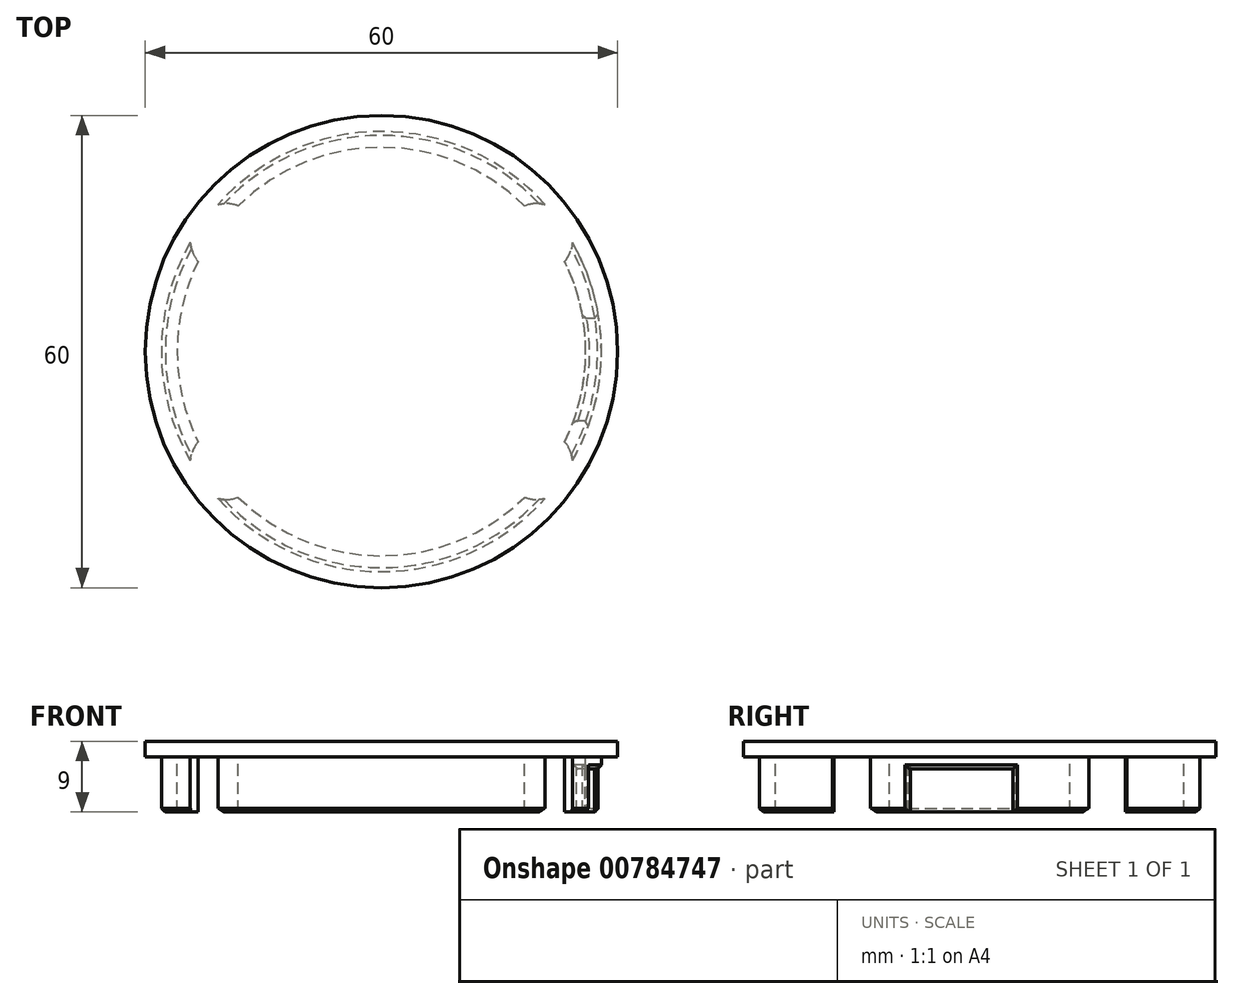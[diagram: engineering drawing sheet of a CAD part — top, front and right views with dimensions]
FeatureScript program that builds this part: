
annotation { "Feature Type Name" : "Feature", "Feature Type Description" : "" }
export const myFeature = defineFeature(function(context is Context, id is Id, definition is map)
    precondition{}
    {
        {
            var Q0;
            Q0=qCreatedBy(makeId("Top.planeOp"),FACE);
            var sketch = newSketch(context, id + "F0", { "sketchPlane" : qUnion([Q0])});
            skLineSegment(sketch, "E0.bottom", {"start": v(-22.5, 17.5) * mm, "end": v(22.5, 17.5) * mm, "construction": true});
            skLineSegment(sketch, "E0.top", {"start": v(-22.5, -17.5) * mm, "end": v(22.5, -17.5) * mm, "construction": true});
            skLineSegment(sketch, "E0.left", {"start": v(-22.5, 17.5) * mm, "end": v(-22.5, -17.5) * mm, "construction": true});
            skLineSegment(sketch, "E0.right", {"start": v(22.5, 17.5) * mm, "end": v(22.5, -17.5) * mm, "construction": true});
            skCircle(sketch, "E1", {"center": v(0, 0) * mm, "radius": 30 * mm});
            skLineSegment(sketch, "E2.bottom", {"start": v(-19.8, -14.3) * mm, "end": v(19.8, -14.3) * mm, "construction": true});
            skLineSegment(sketch, "E2.top", {"start": v(-19.8, 14.3) * mm, "end": v(19.8, 14.3) * mm, "construction": true});
            skLineSegment(sketch, "E2.left", {"start": v(-19.8, -14.3) * mm, "end": v(-19.8, 14.3) * mm, "construction": true});
            skLineSegment(sketch, "E2.right", {"start": v(19.8, -14.3) * mm, "end": v(19.8, 14.3) * mm, "construction": true});
            skSolve(sketch);
        }
        {
            var Q0;
            Q0 = qSketchRegion(id + "F0", true);
            extrude(context, id + "F1", {"entities" : qUnion([Q0]), "depth" : 2 * mm, "offsetDistance" : 25 * mm});
        }
        {
            var Q0;
            Q0=makeQuery(id+"F1.opExtrude","CAP_FACE",FACE,{"disambiguationData":[OSD([sQuery(id+"F0.wireOp",EDGE,"E1")])],"isStart":true});
            var sketch = newSketch(context, id + "F2", { "sketchPlane" : qUnion([Q0])});
            skCircle(sketch, "E3", {"center": v(0, 0) * mm, "radius": 27.95 * mm});
            skSolve(sketch);
        }
        {
            var Q0;
            Q0 = qSketchRegion(id + "F2", true);
            extrude(context, id + "F3", {"entities" : qUnion([Q0]), "operationType" : NewBodyOperationType.ADD, "depth" : 7 * mm, "offsetDistance" : 25 * mm});
        }
        {
            var Q0;
            Q0=makeQuery(id+"F3.opExtrude","CAP_FACE",FACE,{"disambiguationData":[OSD([sQuery(id+"F2.wireOp",EDGE,"E3")])],"isStart":false});
            shell(context, id + "F4", {"entities" : qUnion([Q0]), "thickness" : 2 * mm});
        }
        {
            var Q0;
            Q0=qCreatedBy(makeId("Right.planeOp"),FACE);
            var sketch = newSketch(context, id + "F5", { "sketchPlane" : qUnion([Q0])});
            skLineSegment(sketch, "E4.bottom", {"start": v(4.2, -11.5) * mm, "end": v(-8.8, -11.5) * mm});
            skLineSegment(sketch, "E4.top", {"start": v(4.2, -1.5) * mm, "end": v(-8.8, -1.5) * mm});
            skLineSegment(sketch, "E4.left", {"start": v(4.2, -11.5) * mm, "end": v(4.2, -1.5) * mm});
            skLineSegment(sketch, "E4.right", {"start": v(-8.8, -11.5) * mm, "end": v(-8.8, -1.5) * mm});
            skSolve(sketch);
        }
        {
            var Q0;
            Q0 = qSketchRegion(id + "F5", true);
            extrude(context, id + "F6", {"entities" : qUnion([Q0]), "operationType" : NewBodyOperationType.REMOVE, "depth" : 30 * mm, "offsetDistance" : 25 * mm});
        }
        {
            var Q0;
            Q0=makeQuery(id+"F6.boolean.opBoolean","INTERSECT",EDGE,{"derivedFrom":[makeQuery(id+"F3.opExtrude","SWEPT_FACE",FACE,{"disambiguationData":[OSD([sQuery(id+"F2.wireOp",EDGE,"E3")])]}),makeQuery(id+"F6.opExtrude","SWEPT_FACE",FACE,{"disambiguationData":[OSD([sQuery(id+"F5.wireOp",EDGE,"E4.top")])]})]});
            var Q1;
            Q1=makeQuery(id+"F6.boolean.opBoolean","INTERSECT",EDGE,{"derivedFrom":[makeQuery(id+"F3.opExtrude","SWEPT_FACE",FACE,{"disambiguationData":[OSD([sQuery(id+"F2.wireOp",EDGE,"E3")])]}),makeQuery(id+"F6.opExtrude","SWEPT_FACE",FACE,{"disambiguationData":[OSD([sQuery(id+"F5.wireOp",EDGE,"E4.right")])]})]});
            var Q2;
            Q2=makeQuery(id+"F6.boolean.opBoolean","INTERSECT",EDGE,{"derivedFrom":[makeQuery(id+"F4.opShell","OFFSET_FACE",FACE,{"disambiguationData":[OSD([sQuery(id+"F2.wireOp",EDGE,"E3")])]}),makeQuery(id+"F6.opExtrude","SWEPT_FACE",FACE,{"disambiguationData":[OSD([sQuery(id+"F5.wireOp",EDGE,"E4.top")])]})]});
            var Q3;
            Q3=makeQuery(id+"F6.boolean.opBoolean","INTERSECT",EDGE,{"derivedFrom":[makeQuery(id+"F4.opShell","OFFSET_FACE",FACE,{"disambiguationData":[OSD([sQuery(id+"F2.wireOp",EDGE,"E3")])]}),makeQuery(id+"F6.opExtrude","SWEPT_FACE",FACE,{"disambiguationData":[OSD([sQuery(id+"F5.wireOp",EDGE,"E4.left")])]})]});
            var Q4;
            Q4=makeQuery(id+"F6.boolean.opBoolean","INTERSECT",EDGE,{"derivedFrom":[makeQuery(id+"F4.opShell","OFFSET_FACE",FACE,{"disambiguationData":[OSD([sQuery(id+"F2.wireOp",EDGE,"E3")])]}),makeQuery(id+"F6.opExtrude","SWEPT_FACE",FACE,{"disambiguationData":[OSD([sQuery(id+"F5.wireOp",EDGE,"E4.right")])]})]});
            var Q5;
            Q5=makeQuery(id+"F6.boolean.opBoolean","INTERSECT",EDGE,{"derivedFrom":[makeQuery(id+"F3.opExtrude","SWEPT_FACE",FACE,{"disambiguationData":[OSD([sQuery(id+"F2.wireOp",EDGE,"E3")])]}),makeQuery(id+"F6.opExtrude","SWEPT_FACE",FACE,{"disambiguationData":[OSD([sQuery(id+"F5.wireOp",EDGE,"E4.left")])]})]});
            var Q6;
            Q6=makeQuery(id+"F3.opExtrude","CAP_EDGE",EDGE,{"disambiguationData":[OSD([sQuery(id+"F2.wireOp",EDGE,"E3")])],"isStart":false});
            chamfer(context, id + "F7", {"entities" : qUnion([Q0, Q1, Q2, Q3, Q4, Q5, Q6]), "width" : 0.5 * mm, "tangentPropagation" : true});
        }
        {
            var Q0;
            Q0=makeQuery(id+"F0.imprint","IMPRINT",FACE,{"disambiguationData":[TD([[makeQuery(id+"F0.imprint","IMPRINT",EDGE,{"derivedFrom":sQuery(id+"F0.wireOp",EDGE,"E1")}),1.0]])]});
            var sketch = newSketch(context, id + "F8", { "sketchPlane" : qUnion([Q0])});
            skCircle(sketch, "E5", {"center": v(19.8, -14.3) * mm, "radius": 4.5 * mm});
            skCircle(sketch, "E6.MirrorC", {"center": v(-19.8, -14.3) * mm, "radius": 4.5 * mm});
            skCircle(sketch, "E7.MirrorC", {"center": v(19.8, 14.3) * mm, "radius": 4.5 * mm});
            skCircle(sketch, "E8.MirrorC", {"center": v(-19.8, 14.3) * mm, "radius": 4.5 * mm});
            skSolve(sketch);
        }
        {
            var Q0;
            Q0 = qSketchRegion(id + "F8", true);
            extrude(context, id + "F9", {"entities" : qUnion([Q0]), "operationType" : NewBodyOperationType.REMOVE, "oppositeDirection" : true, "depth" : 25 * mm, "offsetDistance" : 25 * mm});
        }
    });
